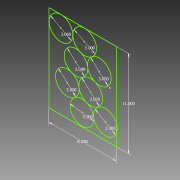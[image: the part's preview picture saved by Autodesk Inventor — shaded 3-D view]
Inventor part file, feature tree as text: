
AUTODESK INVENTOR PART (.ipt)
format: ipt  version: 2015 (Build 190159000, 159)  size: 74,752 bytes
history: native  units: in
note: dims shown in document units (in); Inventor stores cm internally (conversion verified against a paired STEP export)
features: sketch x1
ambient origin geometry x8: Origin, YZ Plane, XZ Plane, XY Plane, X Axis, Y Axis, Z Axis, Center Point
feature tree (1):
  sketch  "Sketch1"  dims[d7=8.5in d8=11.0in d9=3.0in d10=3.0in d11=3.0in d12=3.0in d14=3.0in d16=3.0in d17=3.0in d18=3.0in]
